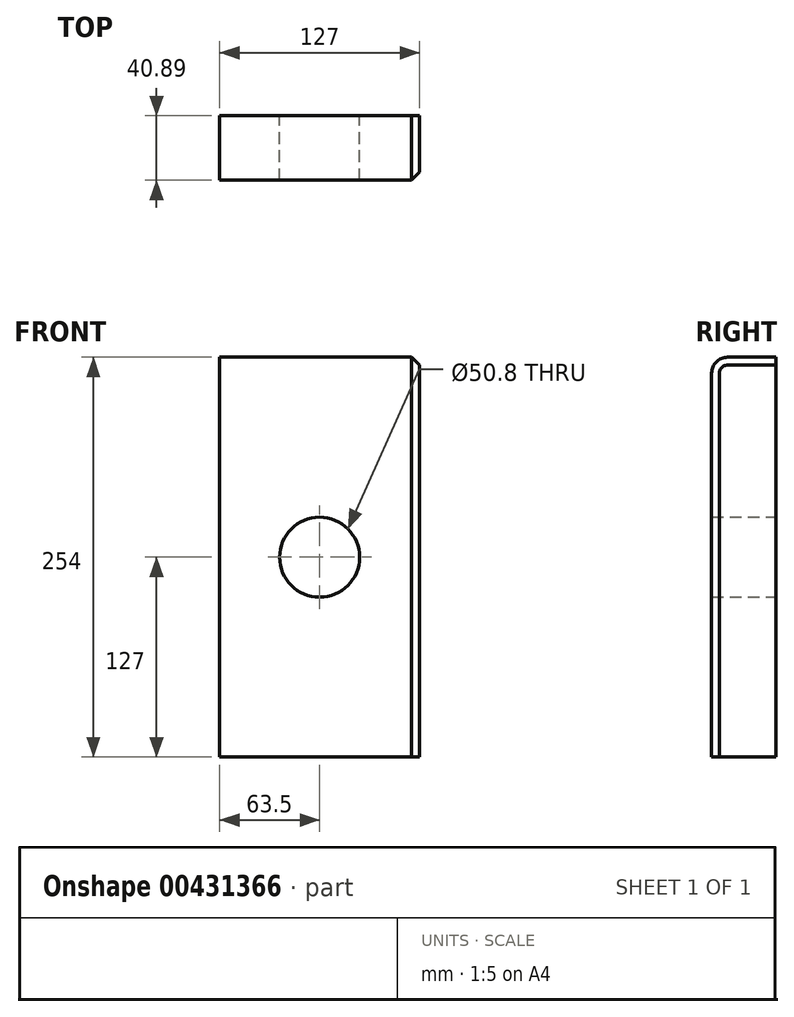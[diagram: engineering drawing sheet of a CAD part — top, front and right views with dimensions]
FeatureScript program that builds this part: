
annotation { "Feature Type Name" : "Feature", "Feature Type Description" : "" }
export const myFeature = defineFeature(function(context is Context, id is Id, definition is map)
    precondition{}
    {
        {
            var Q0;
            Q0=qCreatedBy(makeId("Front.planeOp"),FACE);
            var sketch = newSketch(context, id + "F0", { "sketchPlane" : qUnion([Q0])});
            skLineSegment(sketch, "E0.bottom", {"start": v(63.5, -127) * mm, "end": v(-63.5, -127) * mm});
            skLineSegment(sketch, "E0.top", {"start": v(63.5, 127) * mm, "end": v(-63.5, 127) * mm});
            skLineSegment(sketch, "E0.left", {"start": v(63.5, -127) * mm, "end": v(63.5, 127) * mm});
            skLineSegment(sketch, "E0.right", {"start": v(-63.5, -127) * mm, "end": v(-63.5, 127) * mm});
            skPoint(sketch, "E0.middle", {"position": v(0, 0) * mm});
            skCircle(sketch, "E1", {"center": v(0, 0) * mm, "radius": 25.4 * mm});
            skSolve(sketch);
        }
        {
            var Q0;
            Q0 = qSketchRegion(id + "F0", true);
            extrude(context, id + "F1", {"entities" : qUnion([Q0]), "depth" : 40.9 * mm});
        }
        {
            var Q0;
            Q0=makeQuery(id+"F1.opExtrude","CAP_EDGE",EDGE,{"disambiguationData":[OSD([sQuery(id+"F0.wireOp",EDGE,"E0.top")])],"isStart":false});
            fillet(context, id + "F2", {"entities" : qUnion([Q0]), "radius" : 10 * mm, "tangentPropagation" : true, "allowEdgeOverflow" : false});
        }
        {
            var Q0;
            Q0=makeQuery(id+"F1.opExtrude","CAP_EDGE",EDGE,{"disambiguationData":[OSD([sQuery(id+"F0.wireOp",EDGE,"E0.left")])],"isStart":false});
            chamfer(context, id + "F3", {"entities" : qUnion([Q0]), "width" : 5 * mm, "tangentPropagation" : true});
        }
    });
